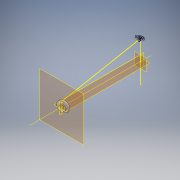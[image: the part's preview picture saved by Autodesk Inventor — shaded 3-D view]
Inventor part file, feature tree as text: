
AUTODESK INVENTOR PART (.ipt)
format: ipt  version: 2018 (Build 220112000, 112)  size: 287,232 bytes
history: native  units: in
note: dims shown in document units (in); Inventor stores cm internally (conversion verified against a paired STEP export)
features: sketch x4, helix x2, plane x1, loft x1, hole x1, other x1, extrude x1, projected_geometry x1
ambient origin geometry x8: Origin, YZ Plane, XZ Plane, XY Plane, X Axis, Y Axis, Z Axis, Center Point
bodies: Solid1 (feature_tree)
feature tree (12):
  sketch  "Sketch1"  dims[d0=2.0in d2=3.9in]
  plane  "Work Plane1"
  loft  "Loft1"
  hole  "Hole1"  [1 undecoded]
  other  "Work Axis2"
  sketch  "Sketch6"  dims[d61=1.0in d62=1.0in d11=0.2in d12=0.75in d13=0.375in d14=0.25in d15=0.5635in d16=1.0in d17=0.8108in d41=0.1in]
  helix  "Coil3"  [1 undecoded]
  helix  "Coil4"  [1 undecoded]
  extrude  "Extrusion2"  Depth=1.0in
  sketch  "Sketch2"  dims[d3=0.5in d5=0.0in d6=90.0deg d7=0.0in d8=90.0deg]
  projected_geometry  "Projected Loop1"
  sketch  "Sketch8"  dims[d42=0.1in d43=0.02in d44=0.195in d45=1.0in d46=7.874in d47=-0.0739in d48=90.0deg d49=90.0deg d50=0.0in d51=0.0in d52=0.195in d53=1.0in d54=7.874in d55=0.0756in d56=90.0deg d57=90.0deg d58=0.0in d59=0.0in d60=3.775in d63=3.0in d64=0.0in]
note: 3 required parameter values undecoded (feature->parameter linkage not recoverable at this tier; creation-order binding heuristic only, values carry confidence <= 0.55)
